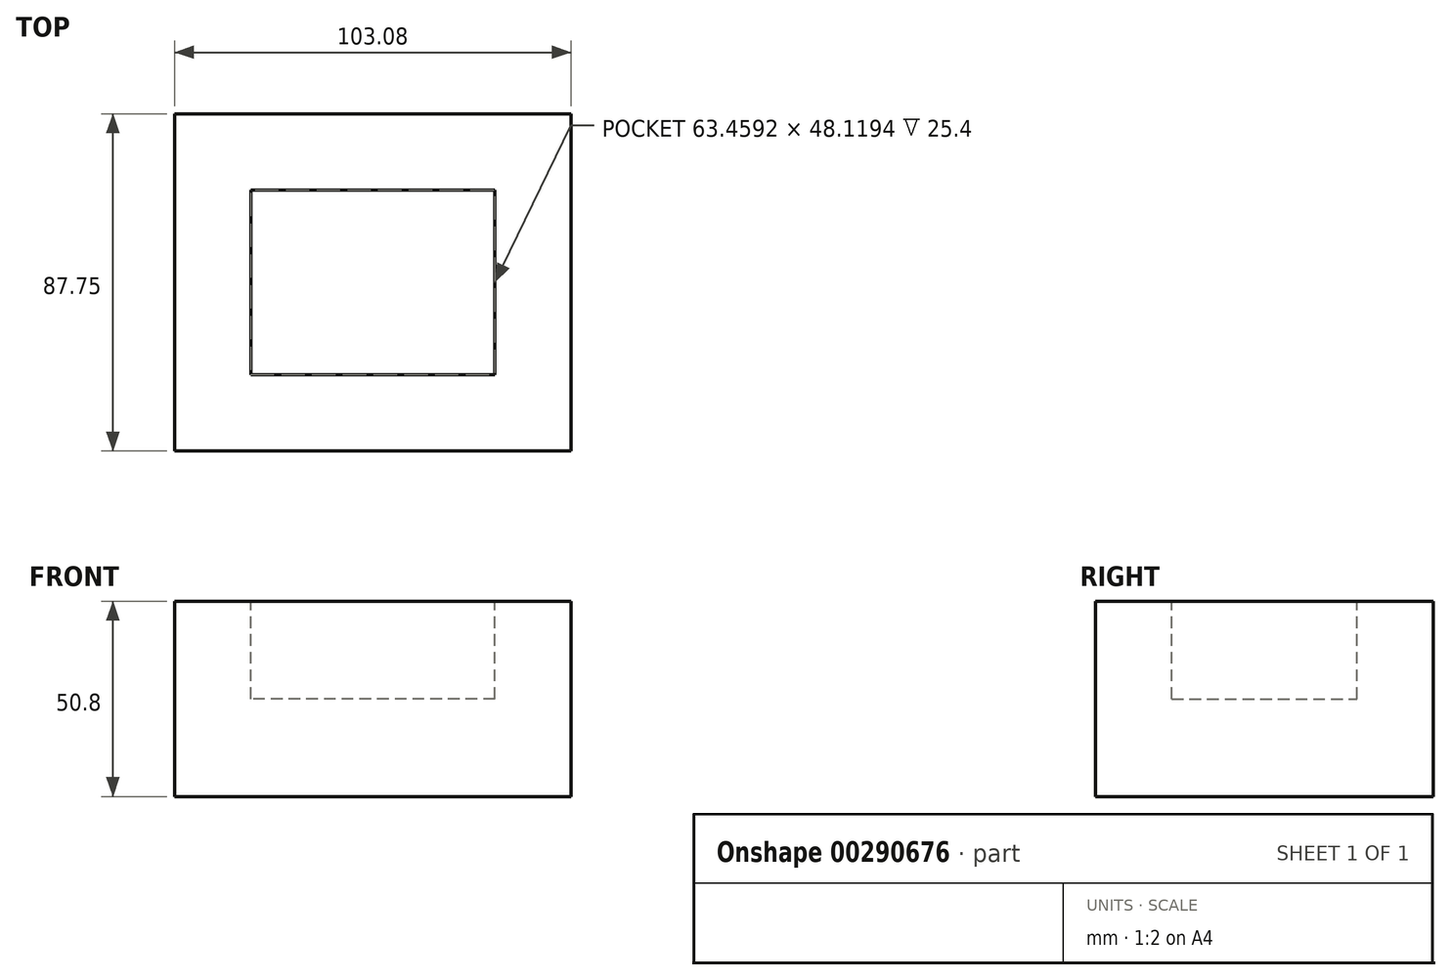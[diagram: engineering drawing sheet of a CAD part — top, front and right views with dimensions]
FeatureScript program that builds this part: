
annotation { "Feature Type Name" : "Feature", "Feature Type Description" : "" }
export const myFeature = defineFeature(function(context is Context, id is Id, definition is map)
    precondition{}
    {
        {
            var Q0;
            Q0=qCreatedBy(makeId("Top.planeOp"),FACE);
            var sketch = newSketch(context, id + "F0", { "sketchPlane" : qUnion([Q0])});
            skLineSegment(sketch, "E0.bottom", {"start": v(50.62, -47.25) * mm, "end": v(-52.46, -47.25) * mm});
            skLineSegment(sketch, "E0.top", {"start": v(50.62, 40.5) * mm, "end": v(-52.46, 40.5) * mm});
            skLineSegment(sketch, "E0.left", {"start": v(50.62, -47.25) * mm, "end": v(50.62, 40.5) * mm});
            skLineSegment(sketch, "E0.right", {"start": v(-52.46, -47.25) * mm, "end": v(-52.46, 40.5) * mm});
            skSolve(sketch);
        }
        {
            var Q0;
            Q0 = qSketchRegion(id + "F0", true);
            extrude(context, id + "F1", {"entities" : qUnion([Q0]), "oppositeDirection" : true, "depth" : 50.8 * mm});
        }
        {
            var Q0;
            Q0=makeQuery(id+"F1.opExtrude","CAP_FACE",FACE,{"disambiguationData":[OSD([sQuery(id+"F0.wireOp",EDGE,"E0.bottom"),sQuery(id+"F0.wireOp",EDGE,"E0.top"),sQuery(id+"F0.wireOp",EDGE,"E0.left"),sQuery(id+"F0.wireOp",EDGE,"E0.right")])],"isStart":true});
            var sketch = newSketch(context, id + "F2", { "sketchPlane" : qUnion([Q0])});
            skLineSegment(sketch, "E1.0", {"start": v(30.8, -27.43) * mm, "end": v(-32.65, -27.43) * mm});
            skLineSegment(sketch, "E1.1", {"start": v(30.8, -27.43) * mm, "end": v(30.8, 20.68) * mm});
            skLineSegment(sketch, "E1.2", {"start": v(30.8, 20.68) * mm, "end": v(-32.65, 20.68) * mm});
            skLineSegment(sketch, "E1.3", {"start": v(-32.65, -27.43) * mm, "end": v(-32.65, 20.68) * mm});
            skSolve(sketch);
        }
        {
            var Q0;
            Q0 = qSketchRegion(id + "F2", true);
            extrude(context, id + "F3", {"entities" : qUnion([Q0]), "operationType" : NewBodyOperationType.REMOVE, "oppositeDirection" : true, "depth" : 25.4 * mm});
        }
    });
